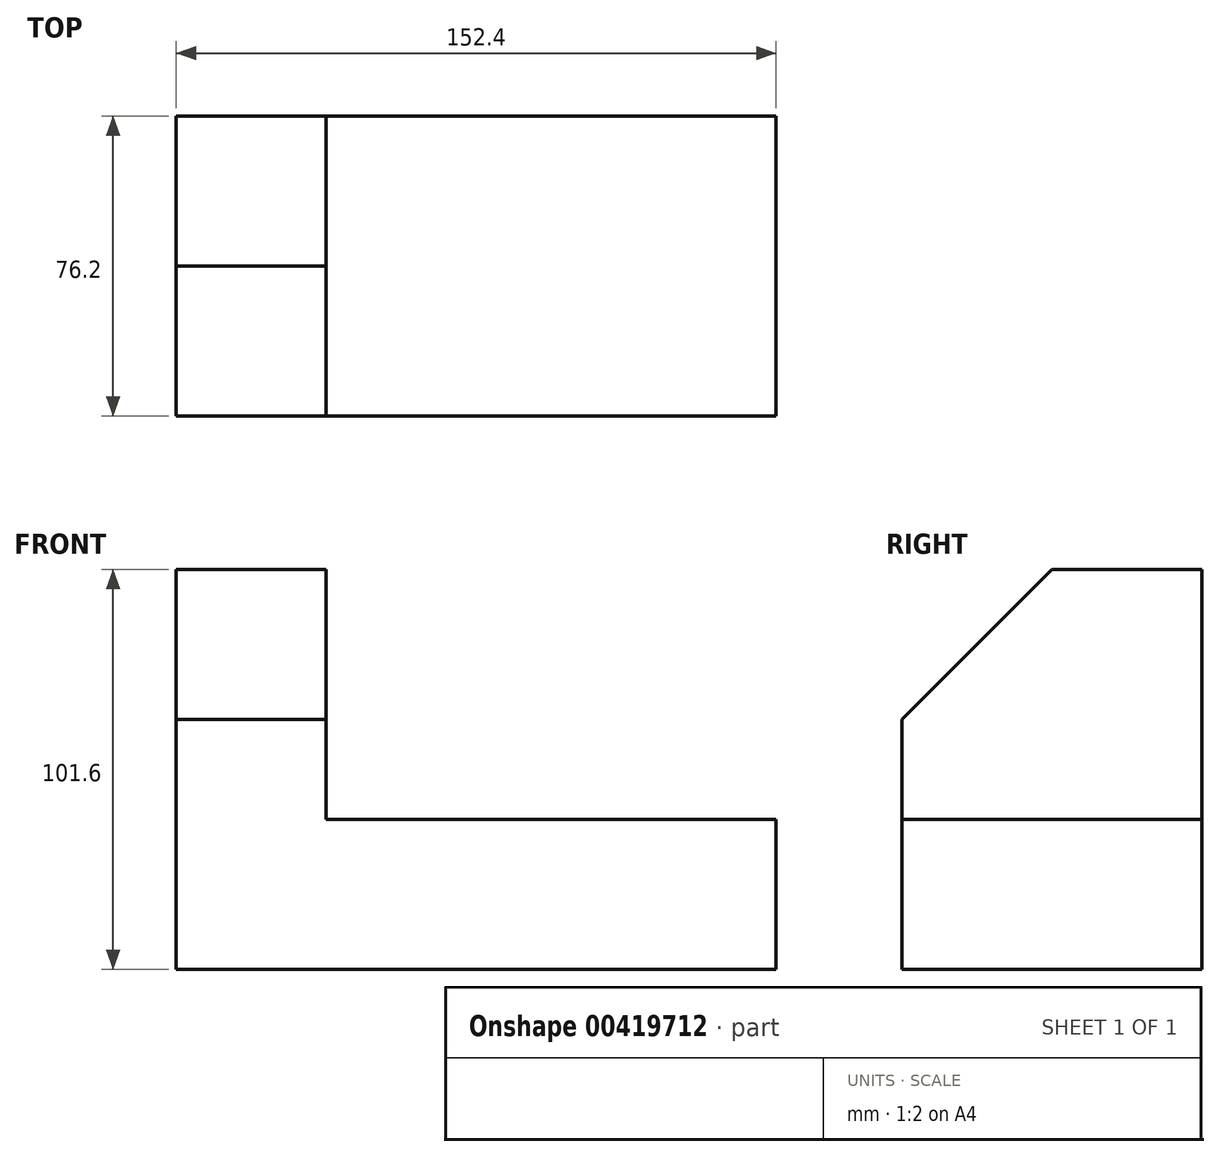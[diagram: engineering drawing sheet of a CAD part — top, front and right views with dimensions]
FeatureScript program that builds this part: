
annotation { "Feature Type Name" : "Feature", "Feature Type Description" : "" }
export const myFeature = defineFeature(function(context is Context, id is Id, definition is map)
    precondition{}
    {
        {
            var Q0;
            Q0=qCreatedBy(makeId("Front.planeOp"),FACE);
            var sketch = newSketch(context, id + "F0", { "sketchPlane" : qUnion([Q0])});
            skLineSegment(sketch, "E0", {"start": v(0, 0) * mm, "end": v(152.4, 0) * mm});
            skLineSegment(sketch, "E1", {"start": v(152.4, 0) * mm, "end": v(152.4, 38.1) * mm});
            skLineSegment(sketch, "E2", {"start": v(152.4, 38.1) * mm, "end": v(38.1, 38.1) * mm});
            skLineSegment(sketch, "E3", {"start": v(38.1, 38.1) * mm, "end": v(38.1, 101.6) * mm});
            skLineSegment(sketch, "E4", {"start": v(38.1, 101.6) * mm, "end": v(0, 101.6) * mm});
            skLineSegment(sketch, "E5", {"start": v(0, 101.6) * mm, "end": v(0, 0) * mm});
            skSolve(sketch);
        }
        {
            var Q0;
            Q0=makeQuery(id+"F0.imprint","IMPRINT",FACE,{"disambiguationData":[TD([[makeQuery(id+"F0.imprint","IMPRINT",EDGE,{"derivedFrom":sQuery(id+"F0.wireOp",EDGE,"E0")}),1.0]])]});
            extrude(context, id + "F1", {"entities" : qUnion([Q0]), "depth" : 76.2 * mm});
        }
        {
            var Q0;
            Q0=makeQuery(id+"F1.opExtrude","SWEPT_FACE",FACE,{"disambiguationData":[OSD([sQuery(id+"F0.wireOp",EDGE,"E3")])]});
            var sketch = newSketch(context, id + "F2", { "sketchPlane" : qUnion([Q0])});
            skLineSegment(sketch, "E6", {"start": v(-38.1, 101.6) * mm, "end": v(-76.2, 63.5) * mm});
            skLineSegment(sketch, "E7", {"start": v(-38.1, 101.6) * mm, "end": v(-76.2, 101.6) * mm});
            skLineSegment(sketch, "E8", {"start": v(-76.2, 101.6) * mm, "end": v(-76.2, 63.5) * mm});
            skSolve(sketch);
        }
        {
            var Q0;
            Q0=makeQuery(id+"F1.opExtrude","SWEPT_FACE",FACE,{"disambiguationData":[OSD([sQuery(id+"F0.wireOp",EDGE,"E2")])]});
            var sketch = newSketch(context, id + "F3", { "sketchPlane" : qUnion([Q0])});
            skSolve(sketch);
        }
        {
            var Q0;
            Q0=makeQuery(id+"F2.imprint","IMPRINT",FACE,{"disambiguationData":[TD([[makeQuery(id+"F2.imprint","IMPRINT",EDGE,{"derivedFrom":sQuery(id+"F2.wireOp",EDGE,"E6")}),-1.0]])]});
            extrude(context, id + "F4", {"entities" : qUnion([Q0]), "operationType" : NewBodyOperationType.REMOVE, "endBound" : BoundingType.THROUGH_ALL, "oppositeDirection" : true, "depth" : 25.4 * mm});
        }
    });
